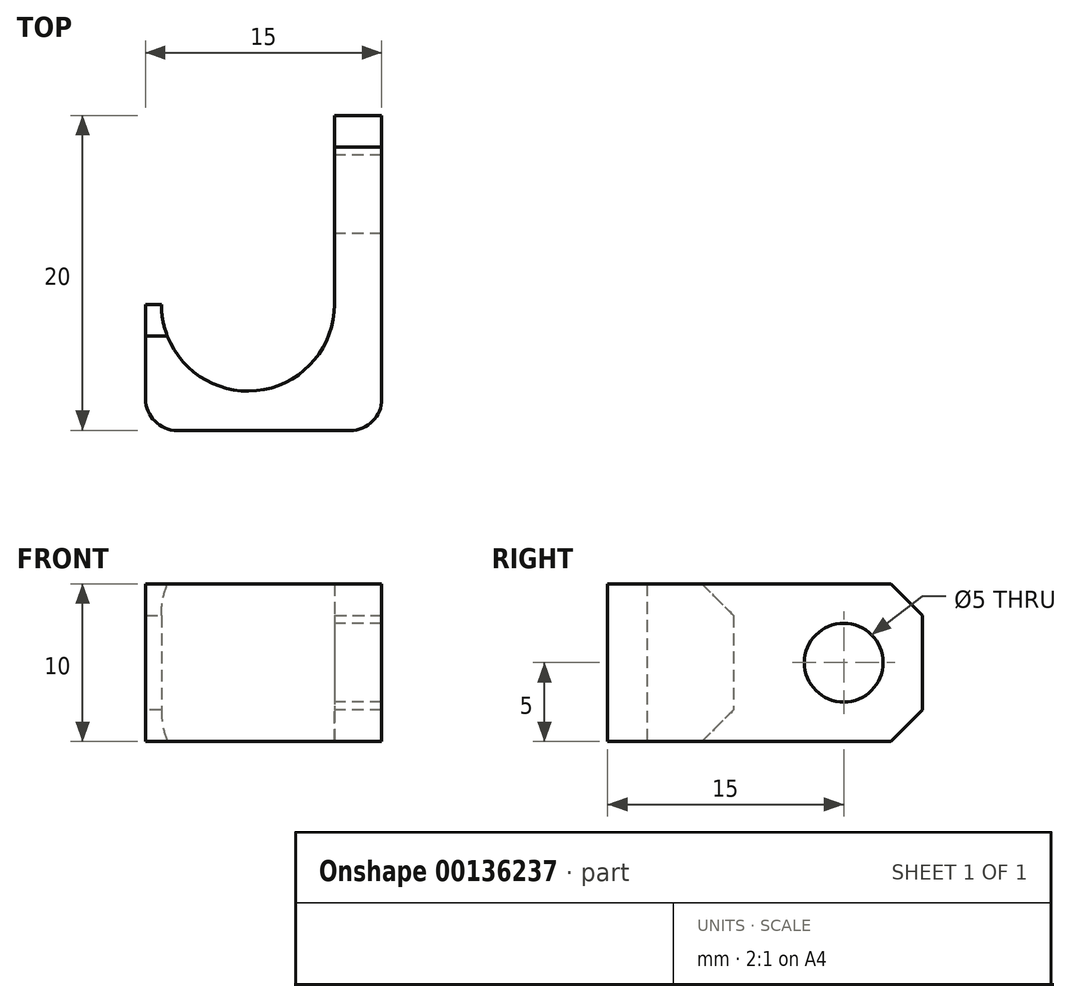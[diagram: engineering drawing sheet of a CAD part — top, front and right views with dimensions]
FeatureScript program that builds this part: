
annotation { "Feature Type Name" : "Feature", "Feature Type Description" : "" }
export const myFeature = defineFeature(function(context is Context, id is Id, definition is map)
    precondition{}
    {
        {
            var Q0;
            Q0=qCreatedBy(makeId("Top.planeOp"),FACE);
            var sketch = newSketch(context, id + "F0", { "sketchPlane" : qUnion([Q0])});
            skLineSegment(sketch, "E0", {"start": v(0, 2) * mm, "end": v(0, 20) * mm});
            skLineSegment(sketch, "E1", {"start": v(0, 20) * mm, "end": v(-3, 20) * mm});
            skLineSegment(sketch, "E2", {"start": v(-3, 20) * mm, "end": v(-3, 8) * mm});
            skLineSegment(sketch, "E3", {"start": v(-15, 8) * mm, "end": v(-15, 2) * mm});
            skLineSegment(sketch, "E4", {"start": v(-2, 0) * mm, "end": v(-13, 0) * mm});
            skArc(sketch, "E5", {"start": v(-14, 8) * mm, "mid": v(-8.5, 2.5) * mm, "end": v(-3, 8) * mm});
            skLineSegment(sketch, "E6.trimOffspring", {"start": v(-14, 8) * mm, "end": v(-15, 8) * mm});
            skPoint(sketch, "E7.visualSharp", {"position": v(0, 0) * mm});
            skArc(sketch, "E7.filletArc", {"start": v(-2, 0) * mm, "mid": v(-0.59, 0.59) * mm, "end": v(0, 2) * mm});
            skPoint(sketch, "E8.visualSharp", {"position": v(-15, 0) * mm});
            skArc(sketch, "E8.filletArc", {"start": v(-15, 2) * mm, "mid": v(-14.41, 0.59) * mm, "end": v(-13, 0) * mm});
            skSolve(sketch);
        }
        {
            var Q0;
            Q0=makeQuery(id+"F0.imprint","IMPRINT",FACE,{"disambiguationData":[TD([[makeQuery(id+"F0.imprint","IMPRINT",EDGE,{"derivedFrom":sQuery(id+"F0.wireOp",EDGE,"E0")}),1.0]])]});
            extrude(context, id + "F1", {"entities" : qUnion([Q0]), "depth" : 10 * mm});
        }
        {
            var Q0;
            Q0=makeQuery(id+"F1.opExtrude","CAP_EDGE",EDGE,{"disambiguationData":[OSD([sQuery(id+"F0.wireOp",EDGE,"E6.trimOffspring")])],"isStart":true});
            var Q1;
            Q1=makeQuery(id+"F1.opExtrude","CAP_EDGE",EDGE,{"disambiguationData":[OSD([sQuery(id+"F0.wireOp",EDGE,"E6.trimOffspring")])],"isStart":false});
            var Q2;
            Q2=makeQuery(id+"F1.opExtrude","CAP_EDGE",EDGE,{"disambiguationData":[OSD([sQuery(id+"F0.wireOp",EDGE,"E1")])],"isStart":true});
            var Q3;
            Q3=makeQuery(id+"F1.opExtrude","CAP_EDGE",EDGE,{"disambiguationData":[OSD([sQuery(id+"F0.wireOp",EDGE,"E1")])],"isStart":false});
            chamfer(context, id + "F2", {"entities" : qUnion([Q0, Q1, Q2, Q3]), "width" : 2 * mm, "tangentPropagation" : true});
        }
        {
            var Q0;
            Q0=makeQuery(id+"F1.opExtrude","SWEPT_FACE",FACE,{"disambiguationData":[OSD([sQuery(id+"F0.wireOp",EDGE,"E2")])]});
            var sketch = newSketch(context, id + "F3", { "sketchPlane" : qUnion([Q0])});
            skCircle(sketch, "E9", {"center": v(-15, 5) * mm, "radius": 2.5 * mm});
            skSolve(sketch);
        }
        {
            var Q0;
            Q0=makeQuery(id+"F3.imprint","IMPRINT",FACE,{"disambiguationData":[TD([[makeQuery(id+"F3.imprint","IMPRINT",EDGE,{"derivedFrom":sQuery(id+"F3.wireOp",EDGE,"E9")}),1.0]])]});
            extrude(context, id + "F4", {"entities" : qUnion([Q0]), "operationType" : NewBodyOperationType.REMOVE, "oppositeDirection" : true, "depth" : 25 * mm});
        }
    });
